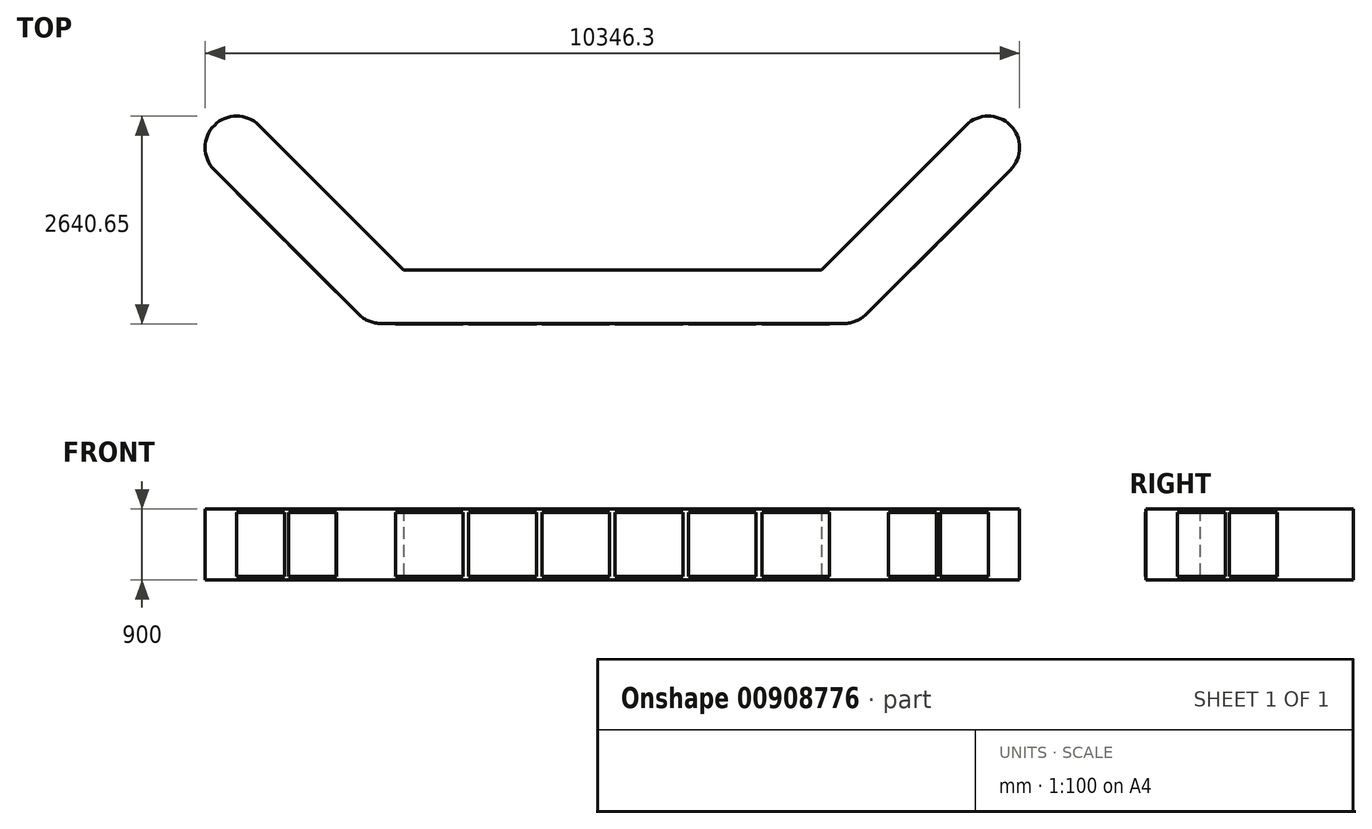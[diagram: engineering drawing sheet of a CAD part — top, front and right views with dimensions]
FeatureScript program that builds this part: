
annotation { "Feature Type Name" : "Feature", "Feature Type Description" : "" }
export const myFeature = defineFeature(function(context is Context, id is Id, definition is map)
    precondition{}
    {
        {
            var Q0;
            Q0=qCreatedBy(makeId("Top.planeOp"),FACE);
            var sketch = newSketch(context, id + "F0", { "sketchPlane" : qUnion([Q0])});
            skCircle(sketch, "E0", {"center": v(0, 0) * mm, "radius": 400 * mm});
            skLineSegment(sketch, "E1", {"start": v(0, 0) * mm, "end": v(-1835.65, 1835.65) * mm, "construction": true});
            skLineSegment(sketch, "E2", {"start": v(0, 0) * mm, "end": v(0, 576.02) * mm, "construction": true});
            skLineSegment(sketch, "E3", {"start": v(-1835.65, 1835.65) * mm, "end": v(-1552.8, 2118.5) * mm});
            skLineSegment(sketch, "E4", {"start": v(-1552.8, 2118.5) * mm, "end": v(282.84, 282.84) * mm});
            skLineSegment(sketch, "E5", {"start": v(282.84, 282.84) * mm, "end": v(-282.84, -282.84) * mm});
            skLineSegment(sketch, "E6", {"start": v(-282.84, -282.84) * mm, "end": v(-2118.5, 1552.8) * mm});
            skLineSegment(sketch, "E7", {"start": v(-2118.5, 1552.8) * mm, "end": v(-1835.65, 1835.65) * mm});
            skCircle(sketch, "E8", {"center": v(5875, 0) * mm, "radius": 400 * mm});
            skLineSegment(sketch, "E9", {"start": v(5875, 0) * mm, "end": v(7710.65, 1835.65) * mm, "construction": true});
            skLineSegment(sketch, "E10", {"start": v(5875, 0) * mm, "end": v(5875, 941.97) * mm, "construction": true});
            skLineSegment(sketch, "E11", {"start": v(7710.65, 1835.65) * mm, "end": v(7993.5, 1552.8) * mm});
            skLineSegment(sketch, "E12", {"start": v(7993.5, 1552.8) * mm, "end": v(6157.84, -282.84) * mm});
            skLineSegment(sketch, "E13", {"start": v(6157.84, -282.84) * mm, "end": v(5592.16, 282.84) * mm, "construction": true});
            skLineSegment(sketch, "E14", {"start": v(5592.16, 282.84) * mm, "end": v(7427.8, 2118.5) * mm});
            skLineSegment(sketch, "E15", {"start": v(7427.8, 2118.5) * mm, "end": v(7710.65, 1835.65) * mm});
            skLineSegment(sketch, "E16", {"start": v(0, -400) * mm, "end": v(5875, -400) * mm});
            skPoint(sketch, "E17", {"position": v(5875, -400) * mm});
            skLineSegment(sketch, "E18", {"start": v(5875, 0) * mm, "end": v(5468.14, 406.86) * mm});
            skLineSegment(sketch, "E19", {"start": v(5468.14, 406.86) * mm, "end": v(6288.82, -413.82) * mm});
            skPoint(sketch, "E20", {"position": v(6157.84, -282.84) * mm});
            skLineSegment(sketch, "E21", {"start": v(0, 0) * mm, "end": v(632.28, 632.28) * mm, "construction": true});
            skLineSegment(sketch, "E22", {"start": v(632.28, 632.28) * mm, "end": v(-619.07, -619.07) * mm, "construction": true});
            skPoint(sketch, "E23", {"position": v(-282.84, -282.84) * mm});
            skLineSegment(sketch, "E24", {"start": v(282.84, 282.84) * mm, "end": v(5592.16, 282.84) * mm});
            skCircle(sketch, "E25", {"center": v(7710.65, 1835.65) * mm, "radius": 400 * mm});
            skCircle(sketch, "E26", {"center": v(-1835.65, 1835.65) * mm, "radius": 400 * mm});
            skSolve(sketch);
        }
        {
            var Q0;
            Q0 = qSketchRegion(id + "F0", true);
            extrude(context, id + "F1", {"entities" : qUnion([Q0]), "depth" : 900 * mm, "offsetDistance" : 25 * mm});
        }
        {
            var Q0;
            Q0=makeQuery(id+"F1.opExtrude","SWEPT_FACE",FACE,{"disambiguationData":[OSD([sQuery(id+"F0.wireOp",EDGE,"E16")])]});
            var sketch = newSketch(context, id + "F2", { "sketchPlane" : qUnion([Q0])});
            skLineSegment(sketch, "E27.bottom", {"start": v(180, 855) * mm, "end": v(1040, 855) * mm});
            skLineSegment(sketch, "E27.top", {"start": v(180, 45) * mm, "end": v(1040, 45) * mm});
            skLineSegment(sketch, "E27.left", {"start": v(180, 855) * mm, "end": v(180, 45) * mm});
            skLineSegment(sketch, "E27.right", {"start": v(1040, 855) * mm, "end": v(1040, 45) * mm});
            skLineSegment(sketch, "E28.bottom", {"start": v(1111, 855) * mm, "end": v(1971, 855) * mm});
            skLineSegment(sketch, "E28.top", {"start": v(1111, 45) * mm, "end": v(1971, 45) * mm});
            skLineSegment(sketch, "E28.left", {"start": v(1111, 855) * mm, "end": v(1111, 45) * mm});
            skLineSegment(sketch, "E28.right", {"start": v(1971, 855) * mm, "end": v(1971, 45) * mm});
            skLineSegment(sketch, "E29.bottom", {"start": v(2042, 855) * mm, "end": v(2902, 855) * mm});
            skLineSegment(sketch, "E29.top", {"start": v(2042, 45) * mm, "end": v(2902, 45) * mm});
            skLineSegment(sketch, "E29.left", {"start": v(2042, 855) * mm, "end": v(2042, 45) * mm});
            skLineSegment(sketch, "E29.right", {"start": v(2902, 855) * mm, "end": v(2902, 45) * mm});
            skLineSegment(sketch, "E30.bottom", {"start": v(2973, 855) * mm, "end": v(3833, 855) * mm});
            skLineSegment(sketch, "E30.top", {"start": v(2973, 45) * mm, "end": v(3833, 45) * mm});
            skLineSegment(sketch, "E30.left", {"start": v(2973, 855) * mm, "end": v(2973, 45) * mm});
            skLineSegment(sketch, "E30.right", {"start": v(3833, 855) * mm, "end": v(3833, 45) * mm});
            skLineSegment(sketch, "E31.bottom", {"start": v(3904, 855) * mm, "end": v(4764, 855) * mm});
            skLineSegment(sketch, "E31.top", {"start": v(3904, 45) * mm, "end": v(4764, 45) * mm});
            skLineSegment(sketch, "E31.left", {"start": v(3904, 855) * mm, "end": v(3904, 45) * mm});
            skLineSegment(sketch, "E31.right", {"start": v(4764, 855) * mm, "end": v(4764, 45) * mm});
            skLineSegment(sketch, "E32.bottom", {"start": v(4835, 855) * mm, "end": v(5695, 855) * mm});
            skLineSegment(sketch, "E32.top", {"start": v(4835, 45) * mm, "end": v(5695, 45) * mm});
            skLineSegment(sketch, "E32.left", {"start": v(4835, 855) * mm, "end": v(4835, 45) * mm});
            skLineSegment(sketch, "E32.right", {"start": v(5695, 855) * mm, "end": v(5695, 45) * mm});
            skLineSegment(sketch, "E33", {"start": v(0, 900) * mm, "end": v(0, -181.84) * mm, "construction": true});
            skLineSegment(sketch, "E34", {"start": v(5875, 900) * mm, "end": v(5875, -295.16) * mm, "construction": true});
            skLineSegment(sketch, "E35", {"start": v(0, 0) * mm, "end": v(180, 45) * mm});
            skLineSegment(sketch, "E36", {"start": v(5875, 0) * mm, "end": v(0, 0) * mm, "construction": true});
            skLineSegment(sketch, "E37", {"start": v(0, 900) * mm, "end": v(5875, 900) * mm, "construction": true});
            skSolve(sketch);
        }
        {
            var Q0;
            Q0 = qSketchRegion(id + "F2", true);
            extrude(context, id + "F3", {"entities" : qUnion([Q0]), "operationType" : NewBodyOperationType.ADD, "depth" : 5 * mm, "offsetDistance" : 25 * mm});
        }
        {
            var Q0;
            Q0=makeQuery(id+"F1.opExtrude","SWEPT_FACE",FACE,{"disambiguationData":[OSD([sQuery(id+"F0.wireOp",EDGE,"E6")])]});
            var sketch = newSketch(context, id + "F4", { "sketchPlane" : qUnion([Q0])});
            skLineSegment(sketch, "E38.bottom", {"start": v(-2193.5, 855) * mm, "end": v(-1333.5, 855) * mm});
            skLineSegment(sketch, "E38.top", {"start": v(-2193.5, 45) * mm, "end": v(-1333.5, 45) * mm});
            skLineSegment(sketch, "E38.left", {"start": v(-2193.5, 855) * mm, "end": v(-2193.5, 45) * mm});
            skLineSegment(sketch, "E38.right", {"start": v(-1333.5, 855) * mm, "end": v(-1333.5, 45) * mm});
            skLineSegment(sketch, "E39.bottom", {"start": v(-1262.5, 855) * mm, "end": v(-402.5, 855) * mm});
            skLineSegment(sketch, "E39.top", {"start": v(-1262.5, 45) * mm, "end": v(-402.5, 45) * mm});
            skLineSegment(sketch, "E39.left", {"start": v(-1262.5, 855) * mm, "end": v(-1262.5, 45) * mm});
            skLineSegment(sketch, "E39.right", {"start": v(-402.5, 855) * mm, "end": v(-402.5, 45) * mm});
            skLineSegment(sketch, "E40", {"start": v(0, 900) * mm, "end": v(0, -363.79) * mm, "construction": true});
            skLineSegment(sketch, "E41", {"start": v(-2596, 900) * mm, "end": v(-2596, -146.71) * mm, "construction": true});
            skSolve(sketch);
        }
        {
            var Q0;
            Q0 = qSketchRegion(id + "F4", true);
            extrude(context, id + "F5", {"entities" : qUnion([Q0]), "operationType" : NewBodyOperationType.ADD, "depth" : 5 * mm, "offsetDistance" : 25 * mm});
        }
        {
            var Q0;
            Q0=makeQuery(id+"F1.opExtrude","SWEPT_FACE",FACE,{"disambiguationData":[OSD([sQuery(id+"F0.wireOp",EDGE,"E12")])]});
            var sketch = newSketch(context, id + "F6", { "sketchPlane" : qUnion([Q0])});
            skLineSegment(sketch, "E42.bottom", {"start": v(4556.75, 855) * mm, "end": v(5416.75, 855) * mm});
            skLineSegment(sketch, "E42.top", {"start": v(4556.75, 45) * mm, "end": v(5416.75, 45) * mm});
            skLineSegment(sketch, "E42.left", {"start": v(4556.75, 855) * mm, "end": v(4556.75, 45) * mm});
            skLineSegment(sketch, "E42.right", {"start": v(5416.75, 855) * mm, "end": v(5416.75, 45) * mm});
            skLineSegment(sketch, "E43.bottom", {"start": v(5487.75, 855) * mm, "end": v(6347.75, 855) * mm});
            skLineSegment(sketch, "E43.top", {"start": v(5487.75, 45) * mm, "end": v(6347.75, 45) * mm});
            skLineSegment(sketch, "E43.left", {"start": v(5487.75, 855) * mm, "end": v(5487.75, 45) * mm});
            skLineSegment(sketch, "E43.right", {"start": v(6347.75, 855) * mm, "end": v(6347.75, 45) * mm});
            skLineSegment(sketch, "E44", {"start": v(6750.25, 900) * mm, "end": v(6750.25, -206.6) * mm, "construction": true});
            skLineSegment(sketch, "E45", {"start": v(4154.25, 900) * mm, "end": v(4154.25, -158.1) * mm, "construction": true});
            skSolve(sketch);
        }
        {
            var Q0;
            Q0 = qSketchRegion(id + "F6", true);
            extrude(context, id + "F7", {"entities" : qUnion([Q0]), "operationType" : NewBodyOperationType.ADD, "depth" : 5 * mm, "offsetDistance" : 25 * mm});
        }
    });
